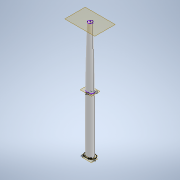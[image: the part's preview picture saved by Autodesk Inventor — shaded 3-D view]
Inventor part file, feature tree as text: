
AUTODESK INVENTOR PART (.ipt)
format: ipt  version: 2022 (Build 260153000, 153)  size: 153,600 bytes
history: native  units: mm
features: sketch x6, plane x3, loft x1
ambient origin geometry x8: Origin, YZ Plane, XZ Plane, XY Plane, X Axis, Y Axis, Z Axis, Center Point
bodies: Body1 (feature_tree)
feature tree (10):
  sketch  "Sketch1"  dims[d0=463.0mm d8=21.0mm]
  plane  "Work Plane1"
  sketch  "Sketch2"  dims[d9=31.0mm]
  plane  "Work Plane3"
  sketch  "Sketch5"  dims[d19=20.0mm]
  sketch  "Sketch6"  dims[d20=30.0mm]
  sketch  "Sketch7"  dims[d25=-455.0mm d26=20.0mm]
  sketch  "Sketch8"  dims[d27=21.0mm d28=31.0mm d29=40.0mm d30=30.0mm d31=10.0mm d32=12.0mm d57=32.0mm d58=33.0mm d59=0.0mm d60=90.0deg d61=0.0mm d62=90.0deg d63=0.0mm d64=90.0deg d12=0.5mm d13=0.872665mm d14=0.5mm d15=0.872665mm]
  loft  "Loft9"
  plane  "Work Plane2"
